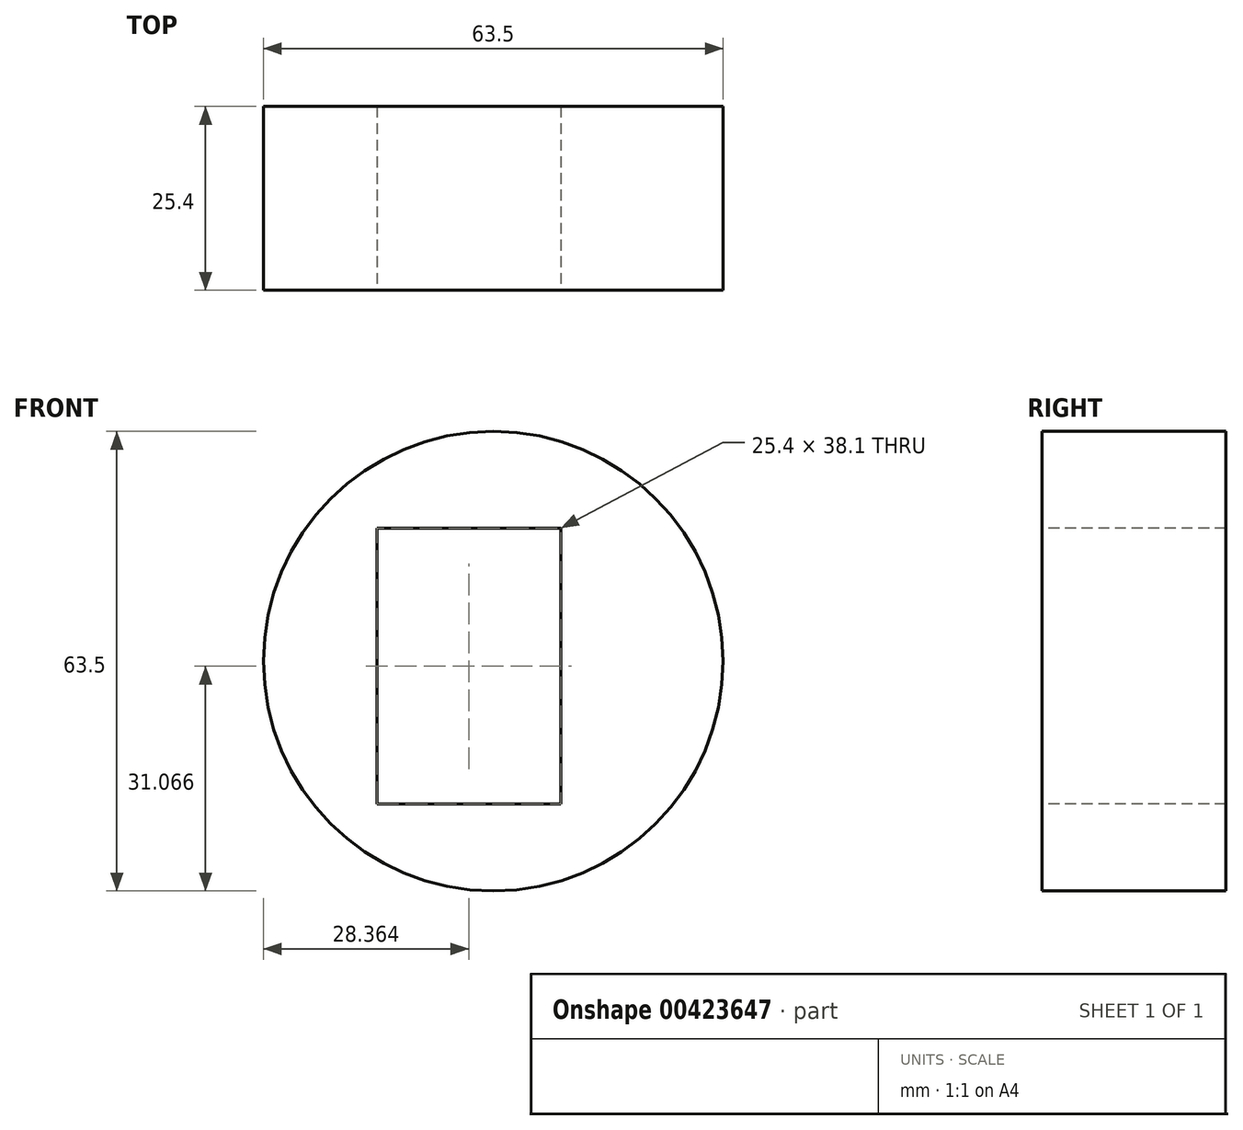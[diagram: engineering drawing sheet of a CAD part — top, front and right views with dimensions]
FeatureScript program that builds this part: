
annotation { "Feature Type Name" : "Feature", "Feature Type Description" : "" }
export const myFeature = defineFeature(function(context is Context, id is Id, definition is map)
    precondition{}
    {
        {
            var Q0;
            Q0=qCreatedBy(makeId("Front.planeOp"),FACE);
            var sketch = newSketch(context, id + "F0", { "sketchPlane" : qUnion([Q0])});
            skCircle(sketch, "E0", {"center": v(-48.73, 9.32) * mm, "radius": 31.75 * mm});
            skSolve(sketch);
        }
        {
            var Q0;
            Q0=makeQuery(id+"F0.imprint","IMPRINT",FACE,{"disambiguationData":[TD([[makeQuery(id+"F0.imprint","IMPRINT",EDGE,{"derivedFrom":sQuery(id+"F0.wireOp",EDGE,"E0")}),1.0]])]});
            extrude(context, id + "F1", {"entities" : qUnion([Q0]), "depth" : 25.4 * mm});
        }
        {
            var Q0;
            Q0=makeQuery(id+"F1.opExtrude","CAP_FACE",FACE,{"disambiguationData":[OSD([sQuery(id+"F0.wireOp",EDGE,"E0")])],"isStart":false});
            var sketch = newSketch(context, id + "F2", { "sketchPlane" : qUnion([Q0])});
            skLineSegment(sketch, "E1.bottom", {"start": v(-64.82, 27.69) * mm, "end": v(-39.42, 27.69) * mm});
            skLineSegment(sketch, "E1.top", {"start": v(-64.82, -10.41) * mm, "end": v(-39.42, -10.41) * mm});
            skLineSegment(sketch, "E1.left", {"start": v(-64.82, 27.69) * mm, "end": v(-64.82, -10.41) * mm});
            skLineSegment(sketch, "E1.right", {"start": v(-39.42, 27.69) * mm, "end": v(-39.42, -10.41) * mm});
            skSolve(sketch);
        }
        {
            var Q0;
            Q0=makeQuery(id+"F2.imprint","IMPRINT",FACE,{"disambiguationData":[TD([[makeQuery(id+"F2.imprint","IMPRINT",EDGE,{"derivedFrom":sQuery(id+"F2.wireOp",EDGE,"E1.bottom")}),1.0]])]});
            extrude(context, id + "F3", {"entities" : qUnion([Q0]), "operationType" : NewBodyOperationType.INTERSECT, "oppositeDirection" : true, "depth" : 31.24 * mm});
        }
    });
